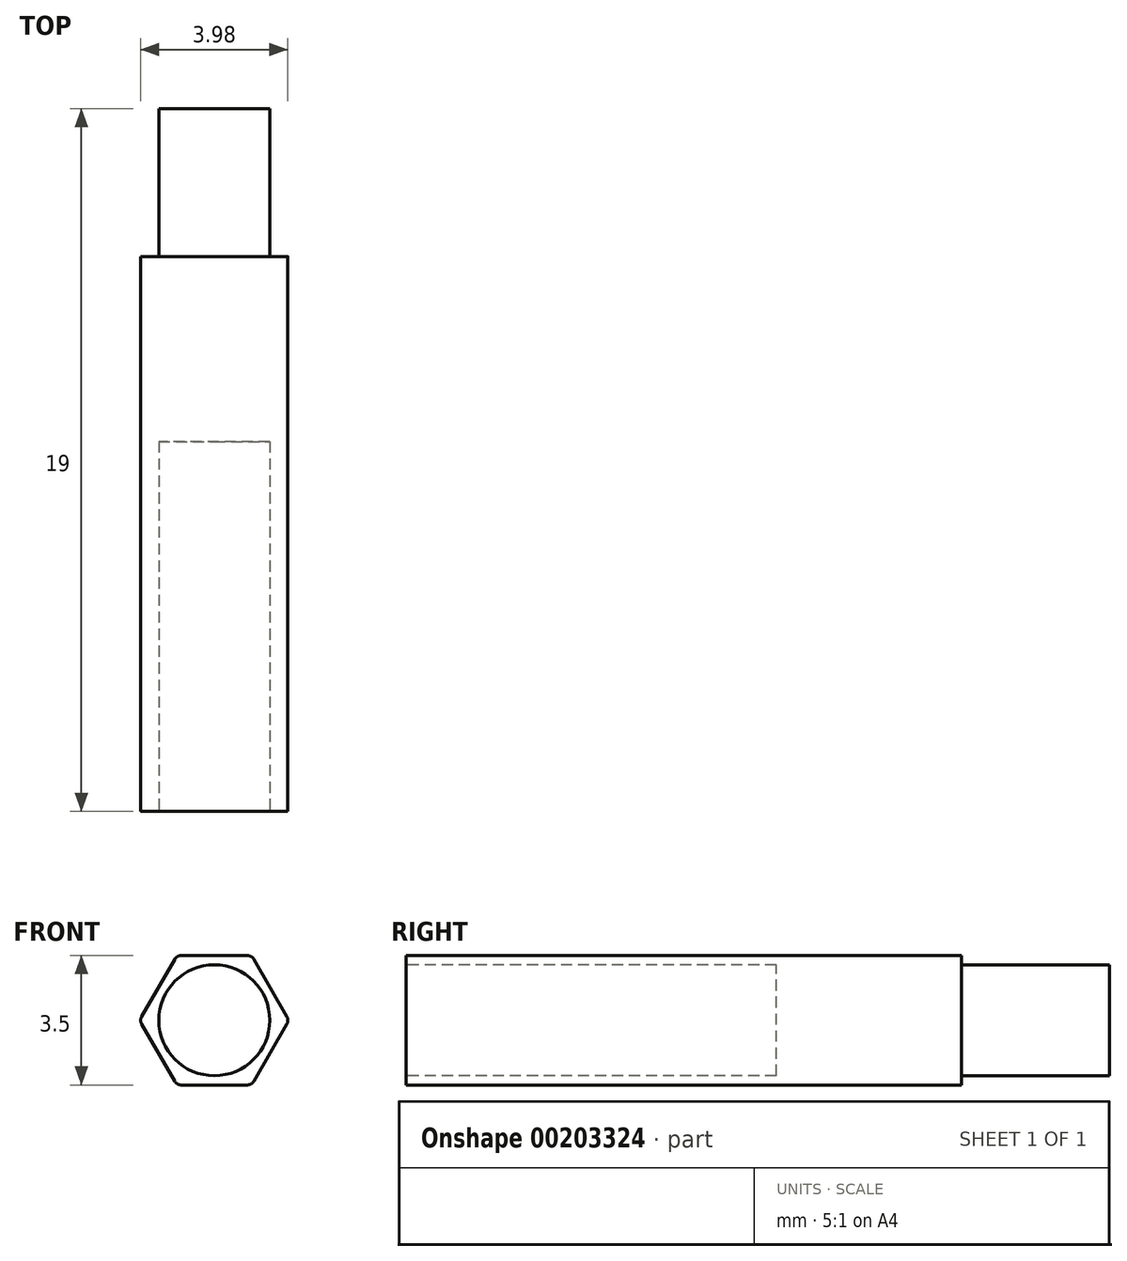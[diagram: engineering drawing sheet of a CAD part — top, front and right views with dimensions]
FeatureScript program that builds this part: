
annotation { "Feature Type Name" : "Feature", "Feature Type Description" : "" }
export const myFeature = defineFeature(function(context is Context, id is Id, definition is map)
    precondition{}
    {
        {
            var Q0;
            Q0=qCreatedBy(makeId("Front.planeOp"),FACE);
            var sketch = newSketch(context, id + "F0", { "sketchPlane" : qUnion([Q0])});
            skCircle(sketch, "E0.cCircle", {"center": v(0, 0) * mm, "radius": 1.75 * mm, "construction": true});
            skLineSegment(sketch, "E0.0", {"start": v(2.02, 0) * mm, "end": v(1.01, -1.75) * mm});
            skLineSegment(sketch, "E0.1", {"start": v(1.01, -1.75) * mm, "end": v(-1.01, -1.75) * mm});
            skLineSegment(sketch, "E0.2", {"start": v(-1.01, -1.75) * mm, "end": v(-2.02, 0) * mm});
            skLineSegment(sketch, "E0.3", {"start": v(-2.02, 0) * mm, "end": v(-1.01, 1.75) * mm});
            skLineSegment(sketch, "E0.4", {"start": v(-1.01, 1.75) * mm, "end": v(1.01, 1.75) * mm});
            skLineSegment(sketch, "E0.5", {"start": v(1.01, 1.75) * mm, "end": v(2.02, 0) * mm});
            skPoint(sketch, "E0.0.midPoint", {"position": v(1.52, -0.87) * mm});
            skLineSegment(sketch, "E1", {"start": v(0, 0) * mm, "end": v(47.32, 0) * mm, "construction": true});
            skSolve(sketch);
        }
        {
            var Q0;
            Q0 = qSketchRegion(id + "F0", true);
            extrude(context, id + "F1", {"entities" : qUnion([Q0]), "depth" : 15 * mm});
        }
        {
            var Q0;
            Q0=makeQuery(id+"F1.opExtrude","SWEPT_EDGE",EDGE,{"disambiguationData":[OSD([sQuery(id+"F0.wireOp",EDGE,"E0.3"),sQuery(id+"F0.wireOp",EDGE,"E0.4")])]});
            var Q1;
            Q1=makeQuery(id+"F1.opExtrude","SWEPT_EDGE",EDGE,{"disambiguationData":[OSD([sQuery(id+"F0.wireOp",EDGE,"E0.4"),sQuery(id+"F0.wireOp",EDGE,"E0.5")])]});
            var Q2;
            Q2=makeQuery(id+"F1.opExtrude","SWEPT_EDGE",EDGE,{"disambiguationData":[OSD([sQuery(id+"F0.wireOp",EDGE,"E0.0"),sQuery(id+"F0.wireOp",EDGE,"E0.5")])]});
            var Q3;
            Q3=makeQuery(id+"F1.opExtrude","SWEPT_EDGE",EDGE,{"disambiguationData":[OSD([sQuery(id+"F0.wireOp",EDGE,"E0.0"),sQuery(id+"F0.wireOp",EDGE,"E0.1")])]});
            var Q4;
            Q4=makeQuery(id+"F1.opExtrude","SWEPT_EDGE",EDGE,{"disambiguationData":[OSD([sQuery(id+"F0.wireOp",EDGE,"E0.1"),sQuery(id+"F0.wireOp",EDGE,"E0.2")])]});
            var Q5;
            Q5=makeQuery(id+"F1.opExtrude","SWEPT_EDGE",EDGE,{"disambiguationData":[OSD([sQuery(id+"F0.wireOp",EDGE,"E0.2"),sQuery(id+"F0.wireOp",EDGE,"E0.3")])]});
            fillet(context, id + "F2", {"entities" : qUnion([Q0, Q1, Q2, Q3, Q4, Q5]), "radius" : 0.2 * mm, "tangentPropagation" : true, "allowEdgeOverflow" : false});
        }
        {
            var Q0;
            Q0=makeQuery(id+"F1.opExtrude","CAP_FACE",FACE,{"disambiguationData":[OSD([sQuery(id+"F0.wireOp",EDGE,"E0.0"),sQuery(id+"F0.wireOp",EDGE,"E0.1"),sQuery(id+"F0.wireOp",EDGE,"E0.2"),sQuery(id+"F0.wireOp",EDGE,"E0.3"),sQuery(id+"F0.wireOp",EDGE,"E0.4"),sQuery(id+"F0.wireOp",EDGE,"E0.5")])],"isStart":false});
            var sketch = newSketch(context, id + "F3", { "sketchPlane" : qUnion([Q0])});
            skCircle(sketch, "E2", {"center": v(0, 0) * mm, "radius": 1.5 * mm});
            skSolve(sketch);
        }
        {
            var Q0;
            Q0 = qSketchRegion(id + "F3", true);
            extrude(context, id + "F4", {"entities" : qUnion([Q0]), "operationType" : NewBodyOperationType.REMOVE, "oppositeDirection" : true, "depth" : 10 * mm});
        }
        {
            var Q0;
            Q0=makeQuery(id+"F1.opExtrude","CAP_FACE",FACE,{"disambiguationData":[OSD([sQuery(id+"F0.wireOp",EDGE,"E0.0"),sQuery(id+"F0.wireOp",EDGE,"E0.1"),sQuery(id+"F0.wireOp",EDGE,"E0.2"),sQuery(id+"F0.wireOp",EDGE,"E0.3"),sQuery(id+"F0.wireOp",EDGE,"E0.4"),sQuery(id+"F0.wireOp",EDGE,"E0.5")])],"isStart":true});
            var sketch = newSketch(context, id + "F5", { "sketchPlane" : qUnion([Q0])});
            skCircle(sketch, "E3", {"center": v(0, 0) * mm, "radius": 1.5 * mm});
            skSolve(sketch);
        }
        {
            var Q0;
            Q0 = qSketchRegion(id + "F5", true);
            extrude(context, id + "F6", {"entities" : qUnion([Q0]), "operationType" : NewBodyOperationType.ADD, "depth" : 4 * mm});
        }
    });
